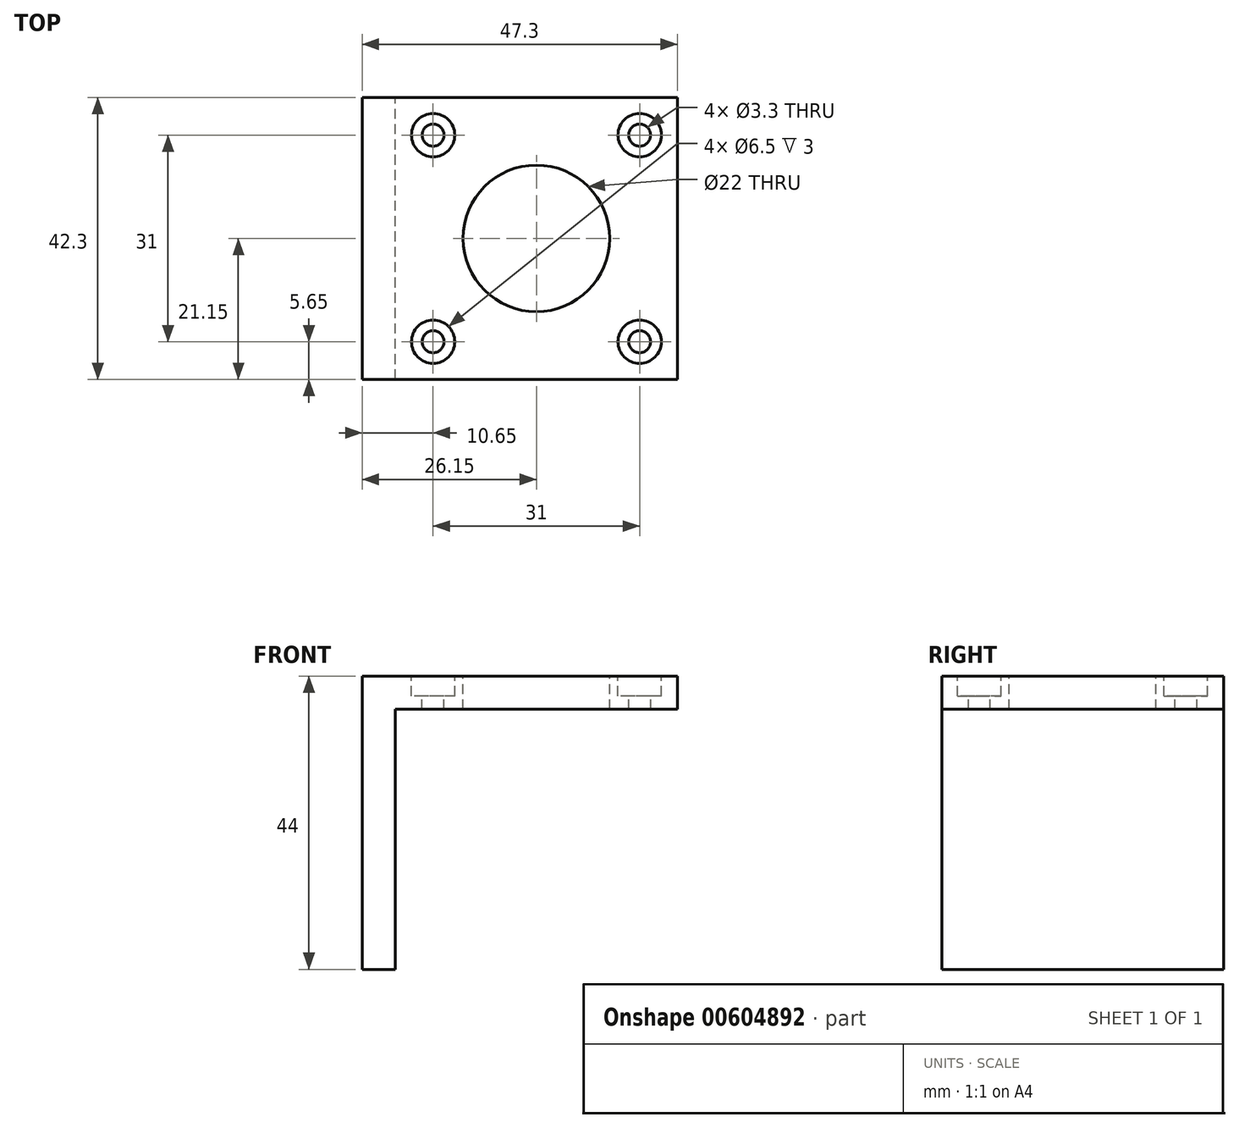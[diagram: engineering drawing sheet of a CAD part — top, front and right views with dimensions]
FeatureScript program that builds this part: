
annotation { "Feature Type Name" : "Feature", "Feature Type Description" : "" }
export const myFeature = defineFeature(function(context is Context, id is Id, definition is map)
    precondition{}
    {
        {
            var Q0;
            Q0=qCreatedBy(makeId("Front.planeOp"),FACE);
            var sketch = newSketch(context, id + "F0", { "sketchPlane" : qUnion([Q0])});
            skLineSegment(sketch, "E0", {"start": v(0, 0) * mm, "end": v(42.3, 0) * mm});
            skLineSegment(sketch, "E1", {"start": v(42.3, 0) * mm, "end": v(42.3, 5) * mm});
            skLineSegment(sketch, "E2", {"start": v(42.3, 5) * mm, "end": v(-5, 5) * mm});
            skLineSegment(sketch, "E3", {"start": v(-5, 5) * mm, "end": v(-5, -39) * mm});
            skLineSegment(sketch, "E4", {"start": v(-5, -39) * mm, "end": v(0, -39) * mm});
            skLineSegment(sketch, "E5", {"start": v(0, -39) * mm, "end": v(0, 0) * mm});
            skSolve(sketch);
        }
        {
            var Q0;
            Q0=makeQuery(id+"F0.imprint","IMPRINT",FACE,{"disambiguationData":[TD([[makeQuery(id+"F0.imprint","IMPRINT",EDGE,{"derivedFrom":sQuery(id+"F0.wireOp",EDGE,"E0")}),1.0]])]});
            extrude(context, id + "F1", {"entities" : qUnion([Q0]), "depth" : 42.3 * mm, "offsetDistance" : 25 * mm});
        }
        {
            var Q0;
            Q0=makeQuery(id+"F1.opExtrude","SWEPT_FACE",FACE,{"disambiguationData":[OSD([sQuery(id+"F0.wireOp",EDGE,"E2")])]});
            var sketch = newSketch(context, id + "F2", { "sketchPlane" : qUnion([Q0])});
            skPoint(sketch, "E6", {"position": v(5.65, -5.65) * mm});
            skPoint(sketch, "E7", {"position": v(36.65, -5.65) * mm});
            skPoint(sketch, "E8", {"position": v(36.65, -36.65) * mm});
            skPoint(sketch, "E9", {"position": v(5.65, -36.65) * mm});
            skPoint(sketch, "E10", {"position": v(21.15, -21.15) * mm});
            skSolve(sketch);
        }
        {
            var Q0;
            Q0=sQuery(id+"F2.wireOp",VERTEX,"E6");
            var Q1;
            Q1=sQuery(id+"F2.wireOp",VERTEX,"E7");
            var Q2;
            Q2=sQuery(id+"F2.wireOp",VERTEX,"E8");
            var Q3;
            Q3=sQuery(id+"F2.wireOp",VERTEX,"E9");
            var Q4;
            Q4=makeQuery(id+"F1.opExtrude","SWEPT_BODY",BODY,{"disambiguationData":[OSD([sQuery(id+"F0.wireOp",EDGE,"E0"),sQuery(id+"F0.wireOp",EDGE,"E1"),sQuery(id+"F0.wireOp",EDGE,"E2"),sQuery(id+"F0.wireOp",EDGE,"E3"),sQuery(id+"F0.wireOp",EDGE,"E4"),sQuery(id+"F0.wireOp",EDGE,"E5")])]});
            hole(context, id + "F3", {"style" : HoleStyle.C_BORE, "endStyle" : HoleEndStyle.BLIND, "standardTappedOrClearance" : lookupTablePath({ "standard" : "ISO", "fit" : "Normal", "size" : "M3", "type" : "Clearance" }), "standardBlindInLast" : lookupTablePath({ "fit" : "Standard", "standard" : "ISO", "size" : "M3", "type" : "Clearance" }), "holeDiameter" : 3.3 * mm, "cBoreDiameter" : 6.5 * mm, "cBoreDepth" : 3 * mm, "majorDiameter" : 5 * mm, "holeDepth" : 10 * mm, "isTappedThrough" : true, "tappedDepth" : 12 * mm, "tapClearance" : 3, "locations" : qUnion([Q0, Q1, Q2, Q3]), "scope" : qUnion([Q4])});
        }
        {
            var Q0;
            Q0=sQuery(id+"F2.wireOp",VERTEX,"E10");
            var Q1;
            Q1=makeQuery(id+"F1.opExtrude","SWEPT_BODY",BODY,{"disambiguationData":[OSD([sQuery(id+"F0.wireOp",EDGE,"E0"),sQuery(id+"F0.wireOp",EDGE,"E1"),sQuery(id+"F0.wireOp",EDGE,"E2"),sQuery(id+"F0.wireOp",EDGE,"E3"),sQuery(id+"F0.wireOp",EDGE,"E4"),sQuery(id+"F0.wireOp",EDGE,"E5")])]});
            hole(context, id + "F4", {"style" : HoleStyle.SIMPLE, "endStyle" : HoleEndStyle.THROUGH, "holeDiameter" : 22 * mm, "majorDiameter" : 5 * mm, "isTappedThrough" : true, "tappedDepth" : 12 * mm, "tapClearance" : 3, "locations" : qUnion([Q0]), "scope" : qUnion([Q1])});
        }
    });
